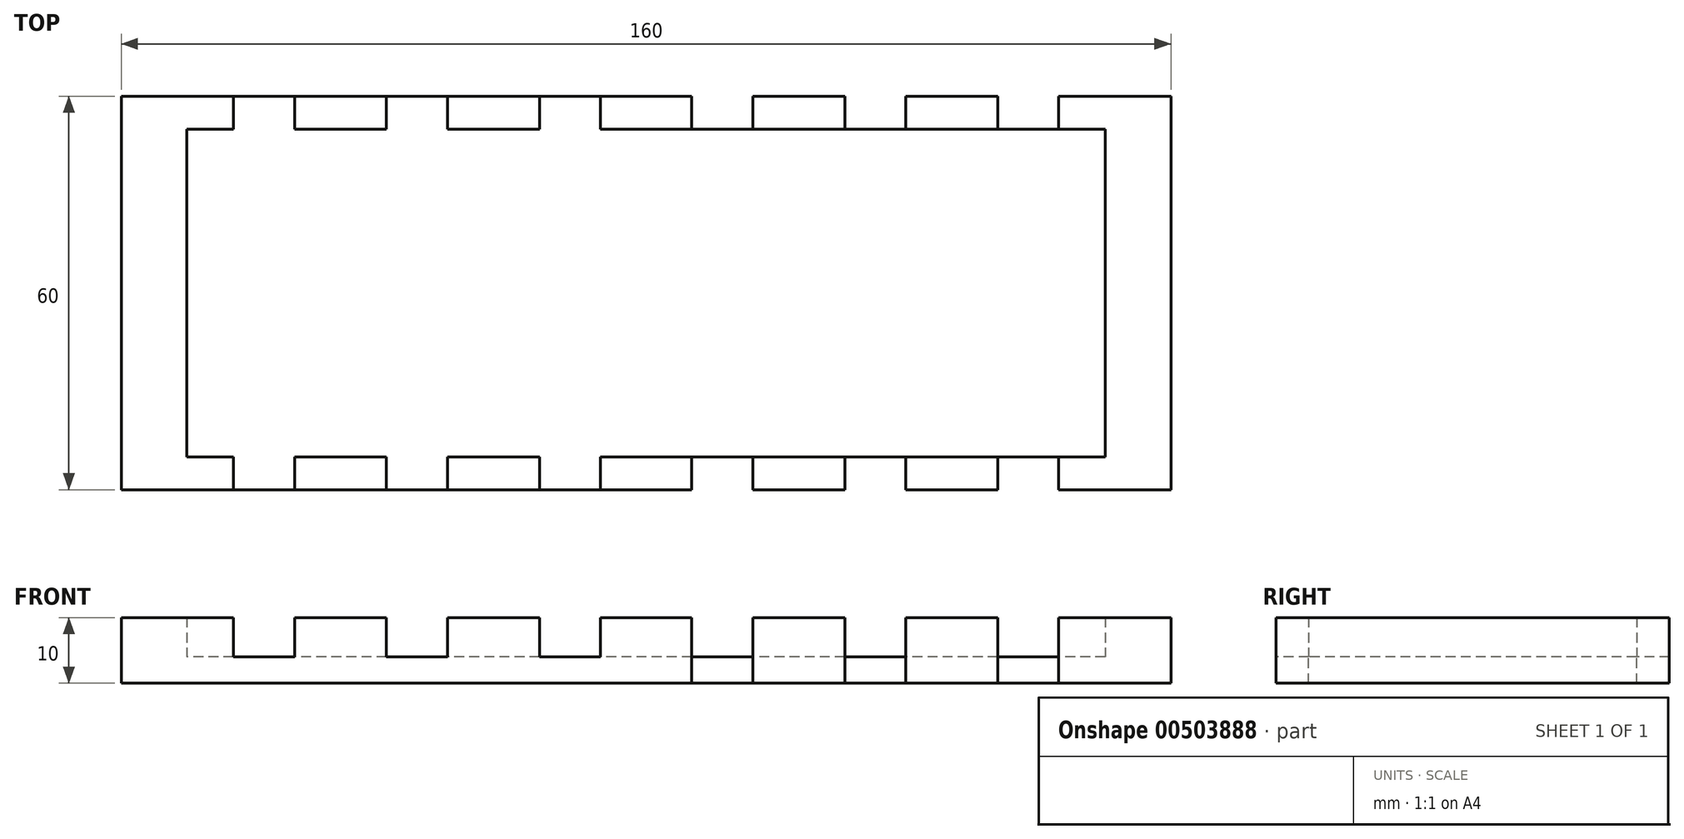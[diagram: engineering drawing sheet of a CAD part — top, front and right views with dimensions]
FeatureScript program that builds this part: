
annotation { "Feature Type Name" : "Feature", "Feature Type Description" : "" }
export const myFeature = defineFeature(function(context is Context, id is Id, definition is map)
    precondition{}
    {
        {
            var Q0;
            Q0=qCreatedBy(makeId("Top.planeOp"),FACE);
            var sketch = newSketch(context, id + "F0", { "sketchPlane" : qUnion([Q0])});
            skLineSegment(sketch, "E0.bottom", {"start": v(80, 30) * mm, "end": v(-80, 30) * mm});
            skLineSegment(sketch, "E0.top", {"start": v(80, -30) * mm, "end": v(-80, -30) * mm});
            skLineSegment(sketch, "E0.left", {"start": v(80, 30) * mm, "end": v(80, -30) * mm});
            skLineSegment(sketch, "E0.right", {"start": v(-80, 30) * mm, "end": v(-80, -30) * mm});
            skPoint(sketch, "E0.middle", {"position": v(0, 0) * mm});
            skLineSegment(sketch, "E1.bottom", {"start": v(70, 25) * mm, "end": v(-70, 25) * mm});
            skLineSegment(sketch, "E1.top", {"start": v(70, -25) * mm, "end": v(-70, -25) * mm});
            skLineSegment(sketch, "E1.left", {"start": v(70, 25) * mm, "end": v(70, -25) * mm});
            skLineSegment(sketch, "E1.right", {"start": v(-70, 25) * mm, "end": v(-70, -25) * mm});
            skLineSegment(sketch, "E2", {"start": v(0, 0) * mm, "end": v(11.6, 0) * mm});
            skLineSegment(sketch, "E3", {"start": v(11.6, 0) * mm, "end": v(34.93, 0) * mm});
            skLineSegment(sketch, "E4", {"start": v(34.93, 0) * mm, "end": v(58.26, 0) * mm});
            skLineSegment(sketch, "E5.bottom", {"start": v(16.25, 30) * mm, "end": v(6.95, 30) * mm});
            skLineSegment(sketch, "E5.top", {"start": v(16.25, -30) * mm, "end": v(6.95, -30) * mm});
            skLineSegment(sketch, "E5.left", {"start": v(16.25, 30) * mm, "end": v(16.25, -30) * mm});
            skLineSegment(sketch, "E5.right", {"start": v(6.95, 30) * mm, "end": v(6.95, -30) * mm});
            skPoint(sketch, "E5.middle", {"position": v(11.6, 0) * mm});
            skLineSegment(sketch, "E6.bottom", {"start": v(39.58, 30) * mm, "end": v(30.28, 30) * mm});
            skLineSegment(sketch, "E6.top", {"start": v(39.58, -30) * mm, "end": v(30.28, -30) * mm});
            skLineSegment(sketch, "E6.left", {"start": v(39.58, 30) * mm, "end": v(39.58, -30) * mm});
            skLineSegment(sketch, "E6.right", {"start": v(30.28, 30) * mm, "end": v(30.28, -30) * mm});
            skPoint(sketch, "E6.middle", {"position": v(34.93, 0) * mm});
            skLineSegment(sketch, "E7.bottom", {"start": v(62.91, 30) * mm, "end": v(53.61, 30) * mm});
            skLineSegment(sketch, "E7.top", {"start": v(62.91, -30) * mm, "end": v(53.61, -30) * mm});
            skLineSegment(sketch, "E7.left", {"start": v(62.91, 30) * mm, "end": v(62.91, -30) * mm});
            skLineSegment(sketch, "E7.right", {"start": v(53.61, 30) * mm, "end": v(53.61, -30) * mm});
            skPoint(sketch, "E7.middle", {"position": v(58.26, 0) * mm});
            skLineSegment(sketch, "E8.MirrorCS", {"start": v(-16.25, 30) * mm, "end": v(-16.25, -30) * mm});
            skLineSegment(sketch, "E9.MirrorCS", {"start": v(-6.95, 30) * mm, "end": v(-6.95, -30) * mm});
            skLineSegment(sketch, "E10.MirrorCS", {"start": v(-30.28, 30) * mm, "end": v(-30.28, -30) * mm});
            skLineSegment(sketch, "E11.MirrorCS", {"start": v(-39.58, 30) * mm, "end": v(-39.58, -30) * mm});
            skLineSegment(sketch, "E12.MirrorCS", {"start": v(-53.61, 30) * mm, "end": v(-53.61, -30) * mm});
            skLineSegment(sketch, "E13.MirrorCS", {"start": v(-62.91, 30) * mm, "end": v(-62.91, -30) * mm});
            skSolve(sketch);
        }
        {
            var Q0;
            {var subQ0=sQuery(id+"F0.wireOp",EDGE,"E8.MirrorCS");var subQ1=sQuery(id+"F0.wireOp",EDGE,"E0.bottom");var subQ2=makeQuery(id+"F0.imprint","INTERSECT",VERTEX,{"derivedFrom":[subQ1,subQ0]});Q0=makeQuery(id+"F0.imprint","IMPRINT",FACE,{"disambiguationData":[TD([[makeQuery(id+"F0.imprint","IMPRINT",EDGE,{"disambiguationData":[TD([[subQ2,-1.0]])],"derivedFrom":subQ1}),1.0]])]});}
            var Q1;
            {var subQ0=sQuery(id+"F0.wireOp",EDGE,"E5.right");var subQ5=sQuery(id+"F0.wireOp",EDGE,"E1.top");var subQ6=makeQuery(id+"F0.imprint","INTERSECT",VERTEX,{"derivedFrom":[subQ5,subQ0]});Q1=makeQuery(id+"F0.imprint","IMPRINT",FACE,{"disambiguationData":[TD([[makeQuery(id+"F0.imprint","IMPRINT",EDGE,{"disambiguationData":[TD([[subQ6,-1.0]])],"derivedFrom":subQ5}),1.0]])]});}
            var Q2;
            {var subQ3=sQuery(id+"F0.wireOp",EDGE,"E7.right");var subQ5=sQuery(id+"F0.wireOp",EDGE,"E1.top");var subQ7=makeQuery(id+"F0.imprint","INTERSECT",VERTEX,{"derivedFrom":[subQ5,subQ3]});Q2=makeQuery(id+"F0.imprint","IMPRINT",FACE,{"disambiguationData":[TD([[makeQuery(id+"F0.imprint","IMPRINT",EDGE,{"disambiguationData":[TD([[subQ7,-1.0]])],"derivedFrom":subQ5}),1.0]])]});}
            var Q3;
            {var subQ0=sQuery(id+"F0.wireOp",EDGE,"E0.right");Q3=makeQuery(id+"F0.imprint","IMPRINT",FACE,{"disambiguationData":[TD([[makeQuery(id+"F0.imprint","IMPRINT",EDGE,{"derivedFrom":subQ0}),1.0]])]});}
            var Q4;
            {var subQ0=sQuery(id+"F0.wireOp",EDGE,"E6.right");var subQ1=sQuery(id+"F0.wireOp",EDGE,"E1.top");var subQ2=makeQuery(id+"F0.imprint","INTERSECT",VERTEX,{"derivedFrom":[subQ1,subQ0]});Q4=makeQuery(id+"F0.imprint","IMPRINT",FACE,{"disambiguationData":[TD([[makeQuery(id+"F0.imprint","IMPRINT",EDGE,{"disambiguationData":[TD([[subQ2,-1.0]])],"derivedFrom":subQ1}),-1.0]])]});}
            var Q5;
            {var subQ5=sQuery(id+"F0.wireOp",EDGE,"E7.top");Q5=makeQuery(id+"F0.imprint","IMPRINT",FACE,{"disambiguationData":[TD([[makeQuery(id+"F0.imprint","IMPRINT",EDGE,{"derivedFrom":subQ5}),-1.0]])]});}
            var Q6;
            {var subQ5=sQuery(id+"F0.wireOp",EDGE,"E6.bottom");Q6=makeQuery(id+"F0.imprint","IMPRINT",FACE,{"disambiguationData":[TD([[makeQuery(id+"F0.imprint","IMPRINT",EDGE,{"derivedFrom":subQ5}),1.0]])]});}
            var Q7;
            {var subQ0=sQuery(id+"F0.wireOp",EDGE,"E8.MirrorCS");var subQ1=sQuery(id+"F0.wireOp",EDGE,"E0.top");var subQ2=makeQuery(id+"F0.imprint","INTERSECT",VERTEX,{"derivedFrom":[subQ1,subQ0]});Q7=makeQuery(id+"F0.imprint","IMPRINT",FACE,{"disambiguationData":[TD([[makeQuery(id+"F0.imprint","IMPRINT",EDGE,{"disambiguationData":[TD([[subQ2,1.0]])],"derivedFrom":subQ1}),-1.0]])]});}
            var Q8;
            {var subQ0=sQuery(id+"F0.wireOp",EDGE,"E1.right");Q8=makeQuery(id+"F0.imprint","IMPRINT",FACE,{"disambiguationData":[TD([[makeQuery(id+"F0.imprint","IMPRINT",EDGE,{"derivedFrom":subQ0}),1.0]])]});}
            var Q9;
            {var subQ3=sQuery(id+"F0.wireOp",EDGE,"E6.right");var subQ5=sQuery(id+"F0.wireOp",EDGE,"E1.bottom");var subQ6=makeQuery(id+"F0.imprint","INTERSECT",VERTEX,{"derivedFrom":[subQ5,subQ3]});Q9=makeQuery(id+"F0.imprint","IMPRINT",FACE,{"disambiguationData":[TD([[makeQuery(id+"F0.imprint","IMPRINT",EDGE,{"disambiguationData":[TD([[subQ6,-1.0]])],"derivedFrom":subQ5}),-1.0]])]});}
            var Q10;
            {var subQ0=sQuery(id+"F0.wireOp",EDGE,"E1.left");Q10=makeQuery(id+"F0.imprint","IMPRINT",FACE,{"disambiguationData":[TD([[makeQuery(id+"F0.imprint","IMPRINT",EDGE,{"derivedFrom":subQ0}),-1.0]])]});}
            var Q11;
            {var subQ0=sQuery(id+"F0.wireOp",EDGE,"E12.MirrorCS");var subQ1=sQuery(id+"F0.wireOp",EDGE,"E0.bottom");var subQ2=makeQuery(id+"F0.imprint","INTERSECT",VERTEX,{"derivedFrom":[subQ1,subQ0]});Q11=makeQuery(id+"F0.imprint","IMPRINT",FACE,{"disambiguationData":[TD([[makeQuery(id+"F0.imprint","IMPRINT",EDGE,{"disambiguationData":[TD([[subQ2,-1.0]])],"derivedFrom":subQ1}),1.0]])]});}
            var Q12;
            {var subQ3=sQuery(id+"F0.wireOp",EDGE,"E7.right");var subQ5=sQuery(id+"F0.wireOp",EDGE,"E1.bottom");var subQ6=makeQuery(id+"F0.imprint","INTERSECT",VERTEX,{"derivedFrom":[subQ5,subQ3]});Q12=makeQuery(id+"F0.imprint","IMPRINT",FACE,{"disambiguationData":[TD([[makeQuery(id+"F0.imprint","IMPRINT",EDGE,{"disambiguationData":[TD([[subQ6,-1.0]])],"derivedFrom":subQ5}),-1.0]])]});}
            var Q13;
            {var subQ0=sQuery(id+"F0.wireOp",EDGE,"E11.MirrorCS");var subQ1=sQuery(id+"F0.wireOp",EDGE,"E0.bottom");var subQ2=makeQuery(id+"F0.imprint","INTERSECT",VERTEX,{"derivedFrom":[subQ1,subQ0]});Q13=makeQuery(id+"F0.imprint","IMPRINT",FACE,{"disambiguationData":[TD([[makeQuery(id+"F0.imprint","IMPRINT",EDGE,{"disambiguationData":[TD([[subQ2,-1.0]])],"derivedFrom":subQ1}),1.0]])]});}
            var Q14;
            {var subQ4=sQuery(id+"F0.wireOp",EDGE,"E0.left");Q14=makeQuery(id+"F0.imprint","IMPRINT",FACE,{"disambiguationData":[TD([[makeQuery(id+"F0.imprint","IMPRINT",EDGE,{"derivedFrom":subQ4}),-1.0]])]});}
            var Q15;
            {var subQ0=sQuery(id+"F0.wireOp",EDGE,"E10.MirrorCS");var subQ1=sQuery(id+"F0.wireOp",EDGE,"E0.bottom");var subQ2=makeQuery(id+"F0.imprint","INTERSECT",VERTEX,{"derivedFrom":[subQ1,subQ0]});Q15=makeQuery(id+"F0.imprint","IMPRINT",FACE,{"disambiguationData":[TD([[makeQuery(id+"F0.imprint","IMPRINT",EDGE,{"disambiguationData":[TD([[subQ2,-1.0]])],"derivedFrom":subQ1}),1.0]])]});}
            var Q16;
            {var subQ5=sQuery(id+"F0.wireOp",EDGE,"E7.bottom");Q16=makeQuery(id+"F0.imprint","IMPRINT",FACE,{"disambiguationData":[TD([[makeQuery(id+"F0.imprint","IMPRINT",EDGE,{"derivedFrom":subQ5}),1.0]])]});}
            var Q17;
            {var subQ5=sQuery(id+"F0.wireOp",EDGE,"E5.bottom");Q17=makeQuery(id+"F0.imprint","IMPRINT",FACE,{"disambiguationData":[TD([[makeQuery(id+"F0.imprint","IMPRINT",EDGE,{"derivedFrom":subQ5}),1.0]])]});}
            var Q18;
            {var subQ0=sQuery(id+"F0.wireOp",EDGE,"E5.right");var subQ5=sQuery(id+"F0.wireOp",EDGE,"E1.bottom");var subQ6=makeQuery(id+"F0.imprint","INTERSECT",VERTEX,{"derivedFrom":[subQ5,subQ0]});Q18=makeQuery(id+"F0.imprint","IMPRINT",FACE,{"disambiguationData":[TD([[makeQuery(id+"F0.imprint","IMPRINT",EDGE,{"disambiguationData":[TD([[subQ6,-1.0]])],"derivedFrom":subQ5}),-1.0]])]});}
            var Q19;
            {var subQ0=sQuery(id+"F0.wireOp",EDGE,"E8.MirrorCS");var subQ1=sQuery(id+"F0.wireOp",EDGE,"E0.top");var subQ2=makeQuery(id+"F0.imprint","INTERSECT",VERTEX,{"derivedFrom":[subQ1,subQ0]});Q19=makeQuery(id+"F0.imprint","IMPRINT",FACE,{"disambiguationData":[TD([[makeQuery(id+"F0.imprint","IMPRINT",EDGE,{"disambiguationData":[TD([[subQ2,-1.0]])],"derivedFrom":subQ1}),-1.0]])]});}
            var Q20;
            {var subQ0=sQuery(id+"F0.wireOp",EDGE,"E8.MirrorCS");var subQ1=sQuery(id+"F0.wireOp",EDGE,"E0.bottom");var subQ2=makeQuery(id+"F0.imprint","INTERSECT",VERTEX,{"derivedFrom":[subQ1,subQ0]});Q20=makeQuery(id+"F0.imprint","IMPRINT",FACE,{"disambiguationData":[TD([[makeQuery(id+"F0.imprint","IMPRINT",EDGE,{"disambiguationData":[TD([[subQ2,1.0]])],"derivedFrom":subQ1}),1.0]])]});}
            var Q21;
            {var subQ3=sQuery(id+"F0.wireOp",EDGE,"E6.right");var subQ5=sQuery(id+"F0.wireOp",EDGE,"E1.top");var subQ6=makeQuery(id+"F0.imprint","INTERSECT",VERTEX,{"derivedFrom":[subQ5,subQ3]});Q21=makeQuery(id+"F0.imprint","IMPRINT",FACE,{"disambiguationData":[TD([[makeQuery(id+"F0.imprint","IMPRINT",EDGE,{"disambiguationData":[TD([[subQ6,-1.0]])],"derivedFrom":subQ5}),1.0]])]});}
            var Q22;
            {var subQ0=sQuery(id+"F0.wireOp",EDGE,"E10.MirrorCS");var subQ1=sQuery(id+"F0.wireOp",EDGE,"E0.top");var subQ2=makeQuery(id+"F0.imprint","INTERSECT",VERTEX,{"derivedFrom":[subQ1,subQ0]});Q22=makeQuery(id+"F0.imprint","IMPRINT",FACE,{"disambiguationData":[TD([[makeQuery(id+"F0.imprint","IMPRINT",EDGE,{"disambiguationData":[TD([[subQ2,-1.0]])],"derivedFrom":subQ1}),-1.0]])]});}
            var Q23;
            {var subQ0=sQuery(id+"F0.wireOp",EDGE,"E11.MirrorCS");var subQ1=sQuery(id+"F0.wireOp",EDGE,"E1.bottom");var subQ2=makeQuery(id+"F0.imprint","INTERSECT",VERTEX,{"derivedFrom":[subQ1,subQ0]});Q23=makeQuery(id+"F0.imprint","IMPRINT",FACE,{"disambiguationData":[TD([[makeQuery(id+"F0.imprint","IMPRINT",EDGE,{"disambiguationData":[TD([[subQ2,-1.0]])],"derivedFrom":subQ1}),1.0]])]});}
            var Q24;
            {var subQ0=sQuery(id+"F0.wireOp",EDGE,"E6.right");var subQ1=sQuery(id+"F0.wireOp",EDGE,"E1.bottom");var subQ2=makeQuery(id+"F0.imprint","INTERSECT",VERTEX,{"derivedFrom":[subQ1,subQ0]});Q24=makeQuery(id+"F0.imprint","IMPRINT",FACE,{"disambiguationData":[TD([[makeQuery(id+"F0.imprint","IMPRINT",EDGE,{"disambiguationData":[TD([[subQ2,-1.0]])],"derivedFrom":subQ1}),1.0]])]});}
            var Q25;
            {var subQ0=sQuery(id+"F0.wireOp",EDGE,"E5.right");var subQ6=sQuery(id+"F0.wireOp",EDGE,"E1.bottom");var subQ7=makeQuery(id+"F0.imprint","INTERSECT",VERTEX,{"derivedFrom":[subQ6,subQ0]});Q25=makeQuery(id+"F0.imprint","IMPRINT",FACE,{"disambiguationData":[TD([[makeQuery(id+"F0.imprint","IMPRINT",EDGE,{"disambiguationData":[TD([[subQ7,-1.0]])],"derivedFrom":subQ6}),1.0]])]});}
            var Q26;
            {var subQ5=sQuery(id+"F0.wireOp",EDGE,"E6.top");Q26=makeQuery(id+"F0.imprint","IMPRINT",FACE,{"disambiguationData":[TD([[makeQuery(id+"F0.imprint","IMPRINT",EDGE,{"derivedFrom":subQ5}),-1.0]])]});}
            var Q27;
            {var subQ0=sQuery(id+"F0.wireOp",EDGE,"E11.MirrorCS");var subQ1=sQuery(id+"F0.wireOp",EDGE,"E0.top");var subQ2=makeQuery(id+"F0.imprint","INTERSECT",VERTEX,{"derivedFrom":[subQ1,subQ0]});Q27=makeQuery(id+"F0.imprint","IMPRINT",FACE,{"disambiguationData":[TD([[makeQuery(id+"F0.imprint","IMPRINT",EDGE,{"disambiguationData":[TD([[subQ2,-1.0]])],"derivedFrom":subQ1}),-1.0]])]});}
            var Q28;
            {var subQ0=sQuery(id+"F0.wireOp",EDGE,"E7.right");var subQ1=sQuery(id+"F0.wireOp",EDGE,"E1.bottom");var subQ2=makeQuery(id+"F0.imprint","INTERSECT",VERTEX,{"derivedFrom":[subQ1,subQ0]});Q28=makeQuery(id+"F0.imprint","IMPRINT",FACE,{"disambiguationData":[TD([[makeQuery(id+"F0.imprint","IMPRINT",EDGE,{"disambiguationData":[TD([[subQ2,-1.0]])],"derivedFrom":subQ1}),1.0]])]});}
            var Q29;
            {var subQ0=sQuery(id+"F0.wireOp",EDGE,"E7.right");var subQ1=sQuery(id+"F0.wireOp",EDGE,"E1.top");var subQ2=makeQuery(id+"F0.imprint","INTERSECT",VERTEX,{"derivedFrom":[subQ1,subQ0]});Q29=makeQuery(id+"F0.imprint","IMPRINT",FACE,{"disambiguationData":[TD([[makeQuery(id+"F0.imprint","IMPRINT",EDGE,{"disambiguationData":[TD([[subQ2,-1.0]])],"derivedFrom":subQ1}),-1.0]])]});}
            var Q30;
            {var subQ0=sQuery(id+"F0.wireOp",EDGE,"E12.MirrorCS");var subQ1=sQuery(id+"F0.wireOp",EDGE,"E0.top");var subQ2=makeQuery(id+"F0.imprint","INTERSECT",VERTEX,{"derivedFrom":[subQ1,subQ0]});Q30=makeQuery(id+"F0.imprint","IMPRINT",FACE,{"disambiguationData":[TD([[makeQuery(id+"F0.imprint","IMPRINT",EDGE,{"disambiguationData":[TD([[subQ2,-1.0]])],"derivedFrom":subQ1}),-1.0]])]});}
            var Q31;
            {var subQ0=sQuery(id+"F0.wireOp",EDGE,"E8.MirrorCS");var subQ1=sQuery(id+"F0.wireOp",EDGE,"E1.bottom");var subQ2=makeQuery(id+"F0.imprint","INTERSECT",VERTEX,{"derivedFrom":[subQ1,subQ0]});Q31=makeQuery(id+"F0.imprint","IMPRINT",FACE,{"disambiguationData":[TD([[makeQuery(id+"F0.imprint","IMPRINT",EDGE,{"disambiguationData":[TD([[subQ2,-1.0]])],"derivedFrom":subQ1}),1.0]])]});}
            var Q32;
            {var subQ5=sQuery(id+"F0.wireOp",EDGE,"E5.top");Q32=makeQuery(id+"F0.imprint","IMPRINT",FACE,{"disambiguationData":[TD([[makeQuery(id+"F0.imprint","IMPRINT",EDGE,{"derivedFrom":subQ5}),-1.0]])]});}
            var Q33;
            {var subQ0=sQuery(id+"F0.wireOp",EDGE,"E12.MirrorCS");var subQ1=sQuery(id+"F0.wireOp",EDGE,"E1.bottom");var subQ2=makeQuery(id+"F0.imprint","INTERSECT",VERTEX,{"derivedFrom":[subQ1,subQ0]});Q33=makeQuery(id+"F0.imprint","IMPRINT",FACE,{"disambiguationData":[TD([[makeQuery(id+"F0.imprint","IMPRINT",EDGE,{"disambiguationData":[TD([[subQ2,-1.0]])],"derivedFrom":subQ1}),1.0]])]});}
            var Q34;
            {var subQ0=sQuery(id+"F0.wireOp",EDGE,"E10.MirrorCS");var subQ1=sQuery(id+"F0.wireOp",EDGE,"E1.bottom");var subQ2=makeQuery(id+"F0.imprint","INTERSECT",VERTEX,{"derivedFrom":[subQ1,subQ0]});Q34=makeQuery(id+"F0.imprint","IMPRINT",FACE,{"disambiguationData":[TD([[makeQuery(id+"F0.imprint","IMPRINT",EDGE,{"disambiguationData":[TD([[subQ2,-1.0]])],"derivedFrom":subQ1}),1.0]])]});}
            var Q35;
            {var subQ0=sQuery(id+"F0.wireOp",EDGE,"E9.MirrorCS");var subQ1=sQuery(id+"F0.wireOp",EDGE,"E1.bottom");var subQ2=makeQuery(id+"F0.imprint","INTERSECT",VERTEX,{"derivedFrom":[subQ1,subQ0]});Q35=makeQuery(id+"F0.imprint","IMPRINT",FACE,{"disambiguationData":[TD([[makeQuery(id+"F0.imprint","IMPRINT",EDGE,{"disambiguationData":[TD([[subQ2,-1.0]])],"derivedFrom":subQ1}),1.0]])]});}
            var Q36;
            {var subQ3=sQuery(id+"F0.wireOp",EDGE,"E5.left");var subQ5=sQuery(id+"F0.wireOp",EDGE,"E1.top");var subQ6=makeQuery(id+"F0.imprint","INTERSECT",VERTEX,{"derivedFrom":[subQ5,subQ3]});Q36=makeQuery(id+"F0.imprint","IMPRINT",FACE,{"disambiguationData":[TD([[makeQuery(id+"F0.imprint","IMPRINT",EDGE,{"disambiguationData":[TD([[subQ6,-1.0]])],"derivedFrom":subQ5}),-1.0]])]});}
            var Q37;
            {var subQ0=sQuery(id+"F0.wireOp",EDGE,"E5.left");var subQ1=sQuery(id+"F0.wireOp",EDGE,"E1.bottom");var subQ2=makeQuery(id+"F0.imprint","INTERSECT",VERTEX,{"derivedFrom":[subQ1,subQ0]});Q37=makeQuery(id+"F0.imprint","IMPRINT",FACE,{"disambiguationData":[TD([[makeQuery(id+"F0.imprint","IMPRINT",EDGE,{"disambiguationData":[TD([[subQ2,-1.0]])],"derivedFrom":subQ1}),1.0]])]});}
            var Q38;
            {var subQ0=sQuery(id+"F0.wireOp",EDGE,"E6.left");var subQ1=sQuery(id+"F0.wireOp",EDGE,"E1.bottom");var subQ2=makeQuery(id+"F0.imprint","INTERSECT",VERTEX,{"derivedFrom":[subQ1,subQ0]});Q38=makeQuery(id+"F0.imprint","IMPRINT",FACE,{"disambiguationData":[TD([[makeQuery(id+"F0.imprint","IMPRINT",EDGE,{"disambiguationData":[TD([[subQ2,-1.0]])],"derivedFrom":subQ1}),1.0]])]});}
            var Q39;
            {var subQ2=sQuery(id+"F0.wireOp",EDGE,"E1.bottom");var subQ4=sQuery(id+"F0.wireOp",EDGE,"E7.left");var subQ5=makeQuery(id+"F0.imprint","INTERSECT",VERTEX,{"derivedFrom":[subQ2,subQ4]});Q39=makeQuery(id+"F0.imprint","IMPRINT",FACE,{"disambiguationData":[TD([[makeQuery(id+"F0.imprint","IMPRINT",EDGE,{"disambiguationData":[TD([[subQ5,-1.0]])],"derivedFrom":subQ2}),1.0]])]});}
            var Q40;
            {var subQ0=sQuery(id+"F0.wireOp",EDGE,"E6.left");var subQ1=sQuery(id+"F0.wireOp",EDGE,"E1.top");var subQ2=makeQuery(id+"F0.imprint","INTERSECT",VERTEX,{"derivedFrom":[subQ1,subQ0]});Q40=makeQuery(id+"F0.imprint","IMPRINT",FACE,{"disambiguationData":[TD([[makeQuery(id+"F0.imprint","IMPRINT",EDGE,{"disambiguationData":[TD([[subQ2,-1.0]])],"derivedFrom":subQ1}),-1.0]])]});}
            extrude(context, id + "F1", {"entities" : qUnion([Q0, Q1, Q2, Q3, Q4, Q5, Q6, Q7, Q8, Q9, Q10, Q11, Q12, Q13, Q14, Q15, Q16, Q17, Q18, Q19, Q20, Q21, Q22, Q23, Q24, Q25, Q26, Q27, Q28, Q29, Q30, Q31, Q32, Q33, Q34, Q35, Q36, Q37, Q38, Q39, Q40]), "oppositeDirection" : true, "depth" : 4 * mm, "offsetDistance" : 25 * mm});
        }
        {
            var Q0;
            {var subQ0=sQuery(id+"F0.wireOp",EDGE,"E0.right");Q0=makeQuery(id+"F0.imprint","IMPRINT",FACE,{"disambiguationData":[TD([[makeQuery(id+"F0.imprint","IMPRINT",EDGE,{"derivedFrom":subQ0}),1.0]])]});}
            var Q1;
            {var subQ0=sQuery(id+"F0.wireOp",EDGE,"E11.MirrorCS");var subQ1=sQuery(id+"F0.wireOp",EDGE,"E0.bottom");var subQ2=makeQuery(id+"F0.imprint","INTERSECT",VERTEX,{"derivedFrom":[subQ1,subQ0]});Q1=makeQuery(id+"F0.imprint","IMPRINT",FACE,{"disambiguationData":[TD([[makeQuery(id+"F0.imprint","IMPRINT",EDGE,{"disambiguationData":[TD([[subQ2,-1.0]])],"derivedFrom":subQ1}),1.0]])]});}
            var Q2;
            {var subQ0=sQuery(id+"F0.wireOp",EDGE,"E11.MirrorCS");var subQ1=sQuery(id+"F0.wireOp",EDGE,"E0.top");var subQ2=makeQuery(id+"F0.imprint","INTERSECT",VERTEX,{"derivedFrom":[subQ1,subQ0]});Q2=makeQuery(id+"F0.imprint","IMPRINT",FACE,{"disambiguationData":[TD([[makeQuery(id+"F0.imprint","IMPRINT",EDGE,{"disambiguationData":[TD([[subQ2,-1.0]])],"derivedFrom":subQ1}),-1.0]])]});}
            var Q3;
            {var subQ0=sQuery(id+"F0.wireOp",EDGE,"E8.MirrorCS");var subQ1=sQuery(id+"F0.wireOp",EDGE,"E0.top");var subQ2=makeQuery(id+"F0.imprint","INTERSECT",VERTEX,{"derivedFrom":[subQ1,subQ0]});Q3=makeQuery(id+"F0.imprint","IMPRINT",FACE,{"disambiguationData":[TD([[makeQuery(id+"F0.imprint","IMPRINT",EDGE,{"disambiguationData":[TD([[subQ2,-1.0]])],"derivedFrom":subQ1}),-1.0]])]});}
            var Q4;
            {var subQ0=sQuery(id+"F0.wireOp",EDGE,"E8.MirrorCS");var subQ1=sQuery(id+"F0.wireOp",EDGE,"E0.bottom");var subQ2=makeQuery(id+"F0.imprint","INTERSECT",VERTEX,{"derivedFrom":[subQ1,subQ0]});Q4=makeQuery(id+"F0.imprint","IMPRINT",FACE,{"disambiguationData":[TD([[makeQuery(id+"F0.imprint","IMPRINT",EDGE,{"disambiguationData":[TD([[subQ2,-1.0]])],"derivedFrom":subQ1}),1.0]])]});}
            var Q5;
            {var subQ0=sQuery(id+"F0.wireOp",EDGE,"E5.right");var subQ5=sQuery(id+"F0.wireOp",EDGE,"E1.bottom");var subQ6=makeQuery(id+"F0.imprint","INTERSECT",VERTEX,{"derivedFrom":[subQ5,subQ0]});Q5=makeQuery(id+"F0.imprint","IMPRINT",FACE,{"disambiguationData":[TD([[makeQuery(id+"F0.imprint","IMPRINT",EDGE,{"disambiguationData":[TD([[subQ6,-1.0]])],"derivedFrom":subQ5}),-1.0]])]});}
            var Q6;
            {var subQ0=sQuery(id+"F0.wireOp",EDGE,"E5.right");var subQ5=sQuery(id+"F0.wireOp",EDGE,"E1.top");var subQ6=makeQuery(id+"F0.imprint","INTERSECT",VERTEX,{"derivedFrom":[subQ5,subQ0]});Q6=makeQuery(id+"F0.imprint","IMPRINT",FACE,{"disambiguationData":[TD([[makeQuery(id+"F0.imprint","IMPRINT",EDGE,{"disambiguationData":[TD([[subQ6,-1.0]])],"derivedFrom":subQ5}),1.0]])]});}
            var Q7;
            {var subQ3=sQuery(id+"F0.wireOp",EDGE,"E6.right");var subQ5=sQuery(id+"F0.wireOp",EDGE,"E1.top");var subQ6=makeQuery(id+"F0.imprint","INTERSECT",VERTEX,{"derivedFrom":[subQ5,subQ3]});Q7=makeQuery(id+"F0.imprint","IMPRINT",FACE,{"disambiguationData":[TD([[makeQuery(id+"F0.imprint","IMPRINT",EDGE,{"disambiguationData":[TD([[subQ6,-1.0]])],"derivedFrom":subQ5}),1.0]])]});}
            var Q8;
            {var subQ3=sQuery(id+"F0.wireOp",EDGE,"E6.right");var subQ5=sQuery(id+"F0.wireOp",EDGE,"E1.bottom");var subQ6=makeQuery(id+"F0.imprint","INTERSECT",VERTEX,{"derivedFrom":[subQ5,subQ3]});Q8=makeQuery(id+"F0.imprint","IMPRINT",FACE,{"disambiguationData":[TD([[makeQuery(id+"F0.imprint","IMPRINT",EDGE,{"disambiguationData":[TD([[subQ6,-1.0]])],"derivedFrom":subQ5}),-1.0]])]});}
            var Q9;
            {var subQ3=sQuery(id+"F0.wireOp",EDGE,"E7.right");var subQ5=sQuery(id+"F0.wireOp",EDGE,"E1.bottom");var subQ6=makeQuery(id+"F0.imprint","INTERSECT",VERTEX,{"derivedFrom":[subQ5,subQ3]});Q9=makeQuery(id+"F0.imprint","IMPRINT",FACE,{"disambiguationData":[TD([[makeQuery(id+"F0.imprint","IMPRINT",EDGE,{"disambiguationData":[TD([[subQ6,-1.0]])],"derivedFrom":subQ5}),-1.0]])]});}
            var Q10;
            {var subQ3=sQuery(id+"F0.wireOp",EDGE,"E7.right");var subQ5=sQuery(id+"F0.wireOp",EDGE,"E1.top");var subQ7=makeQuery(id+"F0.imprint","INTERSECT",VERTEX,{"derivedFrom":[subQ5,subQ3]});Q10=makeQuery(id+"F0.imprint","IMPRINT",FACE,{"disambiguationData":[TD([[makeQuery(id+"F0.imprint","IMPRINT",EDGE,{"disambiguationData":[TD([[subQ7,-1.0]])],"derivedFrom":subQ5}),1.0]])]});}
            var Q11;
            {var subQ4=sQuery(id+"F0.wireOp",EDGE,"E0.left");Q11=makeQuery(id+"F0.imprint","IMPRINT",FACE,{"disambiguationData":[TD([[makeQuery(id+"F0.imprint","IMPRINT",EDGE,{"derivedFrom":subQ4}),-1.0]])]});}
            extrude(context, id + "F2", {"entities" : qUnion([Q0, Q1, Q2, Q3, Q4, Q5, Q6, Q7, Q8, Q9, Q10, Q11]), "operationType" : NewBodyOperationType.ADD, "depth" : 6 * mm, "offsetDistance" : 25 * mm});
        }
    });
